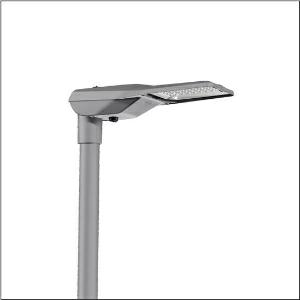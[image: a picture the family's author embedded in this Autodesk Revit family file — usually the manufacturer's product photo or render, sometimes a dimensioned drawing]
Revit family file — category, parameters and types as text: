
# Revit family: streetlight_sl_21_iq_mini___st1_0ab_5xe2m31y08jb_87eb
name_source: partatom
category: Lighting Fixtures
units: mm (PartAtom-declared; Revit-internal decimal feet)

## family parameters
Cut with Voids When Loaded = No
Host = Face
Light Source = No
Part Type = Normal
Room Calculation Point = No
Round Connector Dimension = Use Diameter
Shared = No

## types (1)
- --- (1 x LED, 9870 lm, 72.5 W, 3000K)
    Apparent Load = 73 VA
    CIE Flux Codes = 40 74 97 100 100
    Color Rendering = 70
    Color Temperature = 3000K
    Default Elevation = 1800 mm
    Description = Streetlight SL 21 iQ mini, mast luminaire, primary light control with lens, of PMMA, primary optical cover: cover, of toughened safety glass, transparent, light distribution: ST1.0aB, light emission: direct distribution, primary light characteristic: asymmetric, installation type: post-top, side-entry, LED, High Power LED, rated luminous flux: 9.870lm, luminous efficacy: 136lm/W, light colour: 730, colour temperature: 3000K, control: pre-setting: logarithmic dimming characteristic, Street-Remote, Auto-Match, Temp-Guard, Lumen-Switch, Night-Set, Smart-Wire, Light-Fading, Desk-Remote (wireless, voltage-free reading and setting of iQ features in the workshop via application-optimized NFC function/RFID function), optimised constant luminous flux control (CLO 2.0), mains connection: 220..240V, AC, 50/60Hz, start of lifetime: 73W, end of service life: 76W, reduction: 33W, luminaire housing, of diecast aluminium, powder-coated, Siteco® metallic grey (DB 702S), corrosivity category C5 mid according to DIN EN ISO 12944, please order mast flange separately, inclination adjustable: 0°, 5°, 10°, 15°, sealing non-destructively replaceable, multi-level sealing system, length: 628mm, width: 235mm, height: 110mm, mast flange for spigot size: 42mm (side-entry): 5XC10008XM4, 60/48mm (side-entry/post-top): 5XC10108XM2, 76/60mm (side-entry/post-top): 5XC10108XM1, Smart Interface below and above, protection rating (complete): IP66, insulation class (complete): insulation class II (safety insulation), certification: CE, ENEC, ENEC+, VDE, impact resistance: IK09, permissible operating ambient temperature for outdoor applications: -40..+50°C, standard-compliant lighting for roads and squares, packaging unit: 1 piece

Light Distribution: ST1.0aB
    Height = 110 mm
    Lamp = 1 x LED
    Lamp Light Flux = 9870 lm
    Lamp Power = 72.5 W
    Lamp count = 1
    Length = 625 mm
    Luminous efficacy = 136 lm/W
    Manufacturer = Siteco
    ModVariant = No
    Model = 5XE2M31Y08JB
    Number of Poles = 1
    OnlyDefault = Yes
    Power Factor = 1
    Product Name = Streetlight SL 21 iQ mini | ST1.0aB
    Product group = mast luminaire | pylon top
    ProductGroupID = 6100
    Protection Class = Protection class II
    Protection Degree = IP 66
    RLX_Detail_Level = 1
    RLX_Emergency_Light_Flux = 0 lm
    RLX_Emergency_Type = 0
    RLX_Emergency_Type_DB = No
    RlxData = <blob elided: 92405 chars, md5=40c662c7>
    Socket = socket
    Standby Power = 0 W
    System Light Flux = 9870 lm
    System Power = 73 W
    Type Comments = factory setting: luminous flux: 100 % | dim-lin: 254 | 755 mA
    Type Image = l_1003514.jpg
    URL = http://relux.com
    VarID = @adj_081019
    Voltage = 0 V
    Weight = 0.00 kg
    Width = 234 mm

## geometry (parser evidence)
native form markers: Blend x4, Sweep x10
no freeform markers — native parametric forms only
